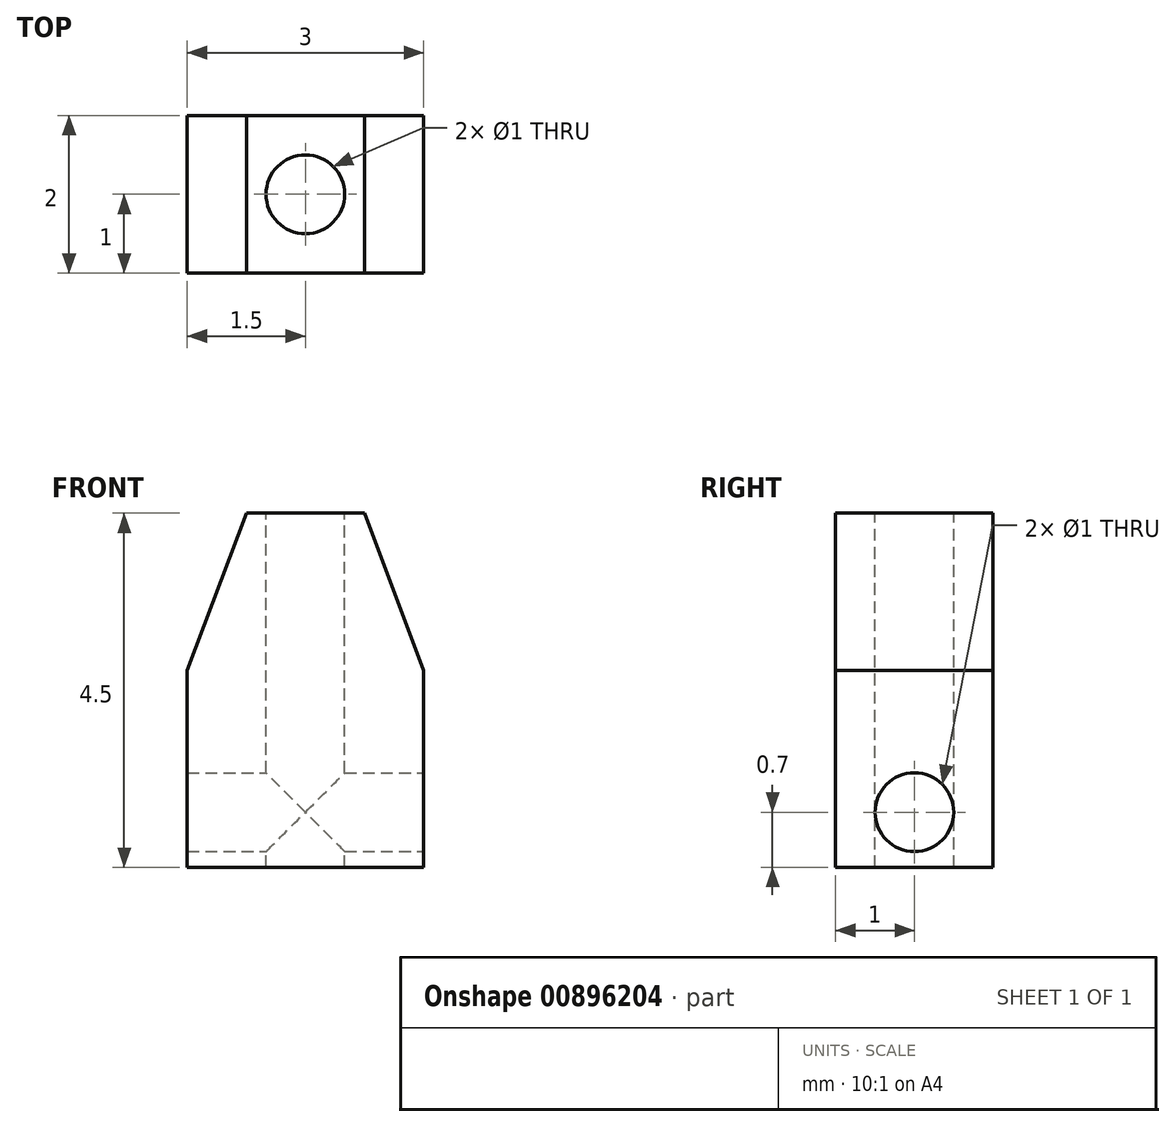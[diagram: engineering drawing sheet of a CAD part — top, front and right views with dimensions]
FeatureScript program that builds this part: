
annotation { "Feature Type Name" : "Feature", "Feature Type Description" : "" }
export const myFeature = defineFeature(function(context is Context, id is Id, definition is map)
    precondition{}
    {
        {
            var Q0;
            Q0=qCreatedBy(makeId("Front.planeOp"),FACE);
            var sketch = newSketch(context, id + "F0", { "sketchPlane" : qUnion([Q0])});
            skLineSegment(sketch, "E0.top", {"start": v(1.5, -1.25) * mm, "end": v(-1.5, -1.25) * mm});
            skLineSegment(sketch, "E0.left", {"start": v(1.5, 1.25) * mm, "end": v(1.5, -1.25) * mm});
            skLineSegment(sketch, "E0.right", {"start": v(-1.5, 1.25) * mm, "end": v(-1.5, -1.25) * mm});
            skPoint(sketch, "E0.middle", {"position": v(0, 0) * mm});
            skLineSegment(sketch, "E1", {"start": v(-0.75, 3.25) * mm, "end": v(0.75, 3.25) * mm});
            skLineSegment(sketch, "E2", {"start": v(-0.75, 3.25) * mm, "end": v(-1.5, 1.25) * mm});
            skLineSegment(sketch, "E3", {"start": v(0.75, 3.25) * mm, "end": v(1.5, 1.25) * mm});
            skSolve(sketch);
        }
        {
            var Q0;
            Q0=makeQuery(id+"F0.imprint","IMPRINT",FACE,{"disambiguationData":[TD([[makeQuery(id+"F0.imprint","IMPRINT",EDGE,{"derivedFrom":sQuery(id+"F0.wireOp",EDGE,"E0.top")}),-1.0]])]});
            extrude(context, id + "F1", {"entities" : qUnion([Q0]), "depth" : 2 * mm, "offsetDistance" : 25 * mm});
        }
        {
            var Q0;
            Q0=makeQuery(id+"F1.opExtrude","SWEPT_FACE",FACE,{"disambiguationData":[OSD([sQuery(id+"F0.wireOp",EDGE,"E0.left")])]});
            var sketch = newSketch(context, id + "F2", { "sketchPlane" : qUnion([Q0])});
            skCircle(sketch, "E4", {"center": v(-1, -0.55) * mm, "radius": 0.5 * mm});
            skSolve(sketch);
        }
        {
            var Q0;
            Q0 = qSketchRegion(id + "F2", true);
            extrude(context, id + "F3", {"entities" : qUnion([Q0]), "operationType" : NewBodyOperationType.REMOVE, "oppositeDirection" : true, "depth" : 25 * mm, "offsetDistance" : 25 * mm});
        }
        {
            var Q0;
            Q0=makeQuery(id+"F1.opExtrude","SWEPT_FACE",FACE,{"disambiguationData":[OSD([sQuery(id+"F0.wireOp",EDGE,"E1")])]});
            var sketch = newSketch(context, id + "F4", { "sketchPlane" : qUnion([Q0])});
            skCircle(sketch, "E5", {"center": v(0, -1) * mm, "radius": 0.5 * mm});
            skSolve(sketch);
        }
        {
            var Q0;
            Q0 = qSketchRegion(id + "F4", true);
            extrude(context, id + "F5", {"entities" : qUnion([Q0]), "operationType" : NewBodyOperationType.REMOVE, "oppositeDirection" : true, "depth" : 25 * mm, "offsetDistance" : 25 * mm});
        }
    });
